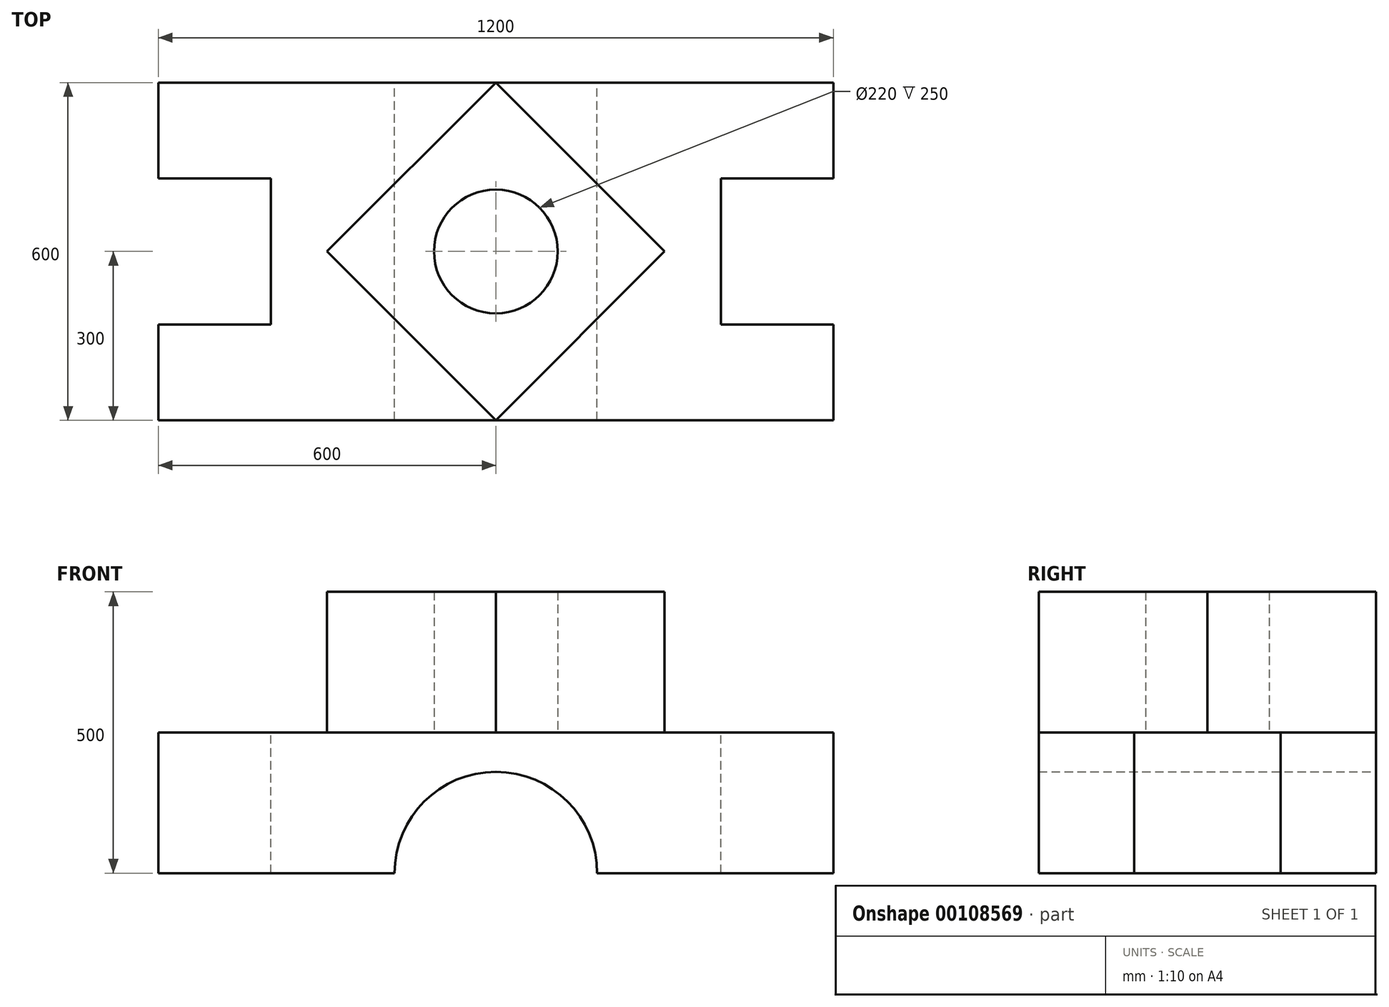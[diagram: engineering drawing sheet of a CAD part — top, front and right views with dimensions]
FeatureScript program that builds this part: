
annotation { "Feature Type Name" : "Feature", "Feature Type Description" : "" }
export const myFeature = defineFeature(function(context is Context, id is Id, definition is map)
    precondition{}
    {
        {
            var Q0;
            Q0=qCreatedBy(makeId("Front.planeOp"),FACE);
            var sketch = newSketch(context, id + "F0", { "sketchPlane" : qUnion([Q0])});
            skLineSegment(sketch, "E0.bottom", {"start": v(-600, 125) * mm, "end": v(600, 125) * mm});
            skLineSegment(sketch, "E0.top", {"start": v(-600, -125) * mm, "end": v(-180, -125) * mm});
            skLineSegment(sketch, "E0.left", {"start": v(-600, 125) * mm, "end": v(-600, -125) * mm});
            skLineSegment(sketch, "E0.right", {"start": v(600, 125) * mm, "end": v(600, -125) * mm});
            skPoint(sketch, "E0.middle", {"position": v(0, 0) * mm});
            skArc(sketch, "E1", {"start": v(180, -125) * mm, "mid": v(0, 55) * mm, "end": v(-180, -125) * mm});
            skLineSegment(sketch, "E2.trimOffspring", {"start": v(180, -125) * mm, "end": v(600, -125) * mm});
            skSolve(sketch);
        }
        {
            var Q0;
            Q0 = qSketchRegion(id + "F0", true);
            extrude(context, id + "F1", {"entities" : qUnion([Q0]), "depth" : 600 * mm});
        }
        {
            var Q0;
            Q0=makeQuery(id+"F1.opExtrude","SWEPT_FACE",FACE,{"disambiguationData":[OSD([sQuery(id+"F0.wireOp",EDGE,"E0.bottom")])]});
            var sketch = newSketch(context, id + "F2", { "sketchPlane" : qUnion([Q0])});
            skLineSegment(sketch, "E3.bottom", {"start": v(-400, -170) * mm, "end": v(-600, -170) * mm});
            skLineSegment(sketch, "E3.top", {"start": v(-400, -430) * mm, "end": v(-600, -430) * mm});
            skLineSegment(sketch, "E3.left", {"start": v(-400, -170) * mm, "end": v(-400, -430) * mm});
            skPoint(sketch, "E3.middle", {"position": v(-600, -300) * mm});
            skLineSegment(sketch, "E4.bottom", {"start": v(400, -170) * mm, "end": v(600, -170) * mm});
            skLineSegment(sketch, "E4.top", {"start": v(400, -430) * mm, "end": v(600, -430) * mm});
            skLineSegment(sketch, "E4.left", {"start": v(400, -170) * mm, "end": v(400, -430) * mm});
            skPoint(sketch, "E4.middle", {"position": v(600, -300) * mm});
            skPoint(sketch, "E4.right.start.orphan", {"position": v(800, -170) * mm});
            skPoint(sketch, "E5.orphan", {"position": v(800, -430) * mm});
            skSolve(sketch);
        }
        {
            var Q0;
            {var subQ0=sQuery(id+"F2.wireOp",EDGE,"E3.bottom");Q0=makeQuery(id+"F2.imprint","IMPRINT",FACE,{"disambiguationData":[TD([[makeQuery(id+"F2.imprint","IMPRINT",EDGE,{"derivedFrom":subQ0}),1.0]])]});}
            var Q1;
            {var subQ0=sQuery(id+"F2.wireOp",EDGE,"E4.bottom");Q1=makeQuery(id+"F2.imprint","IMPRINT",FACE,{"disambiguationData":[TD([[makeQuery(id+"F2.imprint","IMPRINT",EDGE,{"derivedFrom":subQ0}),-1.0]])]});}
            extrude(context, id + "F3", {"entities" : qUnion([Q0, Q1]), "operationType" : NewBodyOperationType.REMOVE, "endBound" : BoundingType.THROUGH_ALL, "oppositeDirection" : true, "depth" : 25.4 * mm});
        }
        {
            var Q0;
            Q0=makeQuery(id+"F1.opExtrude","SWEPT_FACE",FACE,{"disambiguationData":[OSD([sQuery(id+"F0.wireOp",EDGE,"E0.bottom")])]});
            var sketch = newSketch(context, id + "F4", { "sketchPlane" : qUnion([Q0])});
            skCircle(sketch, "E6", {"center": v(0, -300) * mm, "radius": 110 * mm});
            skPoint(sketch, "E6.centerSnap0", {"position": v(400, -300) * mm});
            skLineSegment(sketch, "E7.bottom", {"start": v(300, 0) * mm, "end": v(-300, 0) * mm});
            skLineSegment(sketch, "E7.top", {"start": v(300, -600) * mm, "end": v(-300, -600) * mm});
            skLineSegment(sketch, "E7.left", {"start": v(300, 0) * mm, "end": v(300, -600) * mm});
            skLineSegment(sketch, "E7.right", {"start": v(-300, 0) * mm, "end": v(-300, -600) * mm});
            skLineSegment(sketch, "E8", {"start": v(-300, -300) * mm, "end": v(0, 0) * mm});
            skLineSegment(sketch, "E9", {"start": v(0, 0) * mm, "end": v(300, -300) * mm});
            skLineSegment(sketch, "E10", {"start": v(300, -300) * mm, "end": v(0, -600) * mm});
            skLineSegment(sketch, "E11", {"start": v(0, -600) * mm, "end": v(-300, -300) * mm});
            skSolve(sketch);
        }
        {
            var Q0;
            Q0=makeQuery(id+"F4.imprint","IMPRINT",FACE,{"disambiguationData":[TD([[makeQuery(id+"F4.imprint","IMPRINT",EDGE,{"derivedFrom":sQuery(id+"F4.wireOp",EDGE,"E6")}),-1.0]])]});
            extrude(context, id + "F5", {"entities" : qUnion([Q0]), "operationType" : NewBodyOperationType.ADD, "depth" : 250 * mm});
        }
    });
